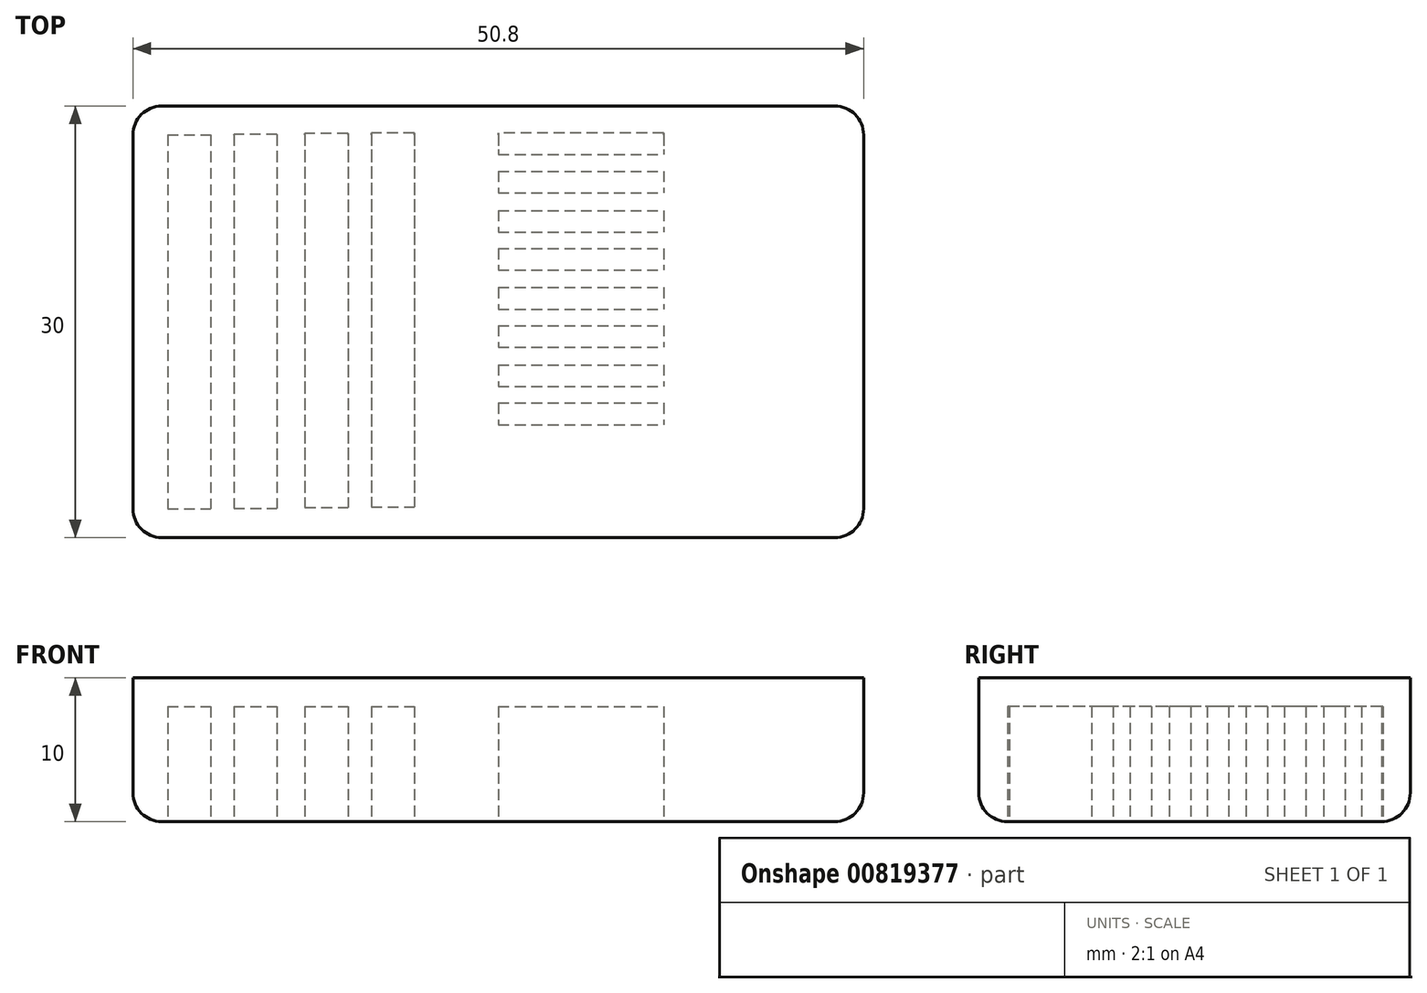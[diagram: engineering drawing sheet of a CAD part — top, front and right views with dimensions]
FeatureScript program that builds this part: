
annotation { "Feature Type Name" : "Feature", "Feature Type Description" : "" }
export const myFeature = defineFeature(function(context is Context, id is Id, definition is map)
    precondition{}
    {
        {
            var Q0;
            Q0=qCreatedBy(makeId("Top.planeOp"),FACE);
            var sketch = newSketch(context, id + "F0", { "sketchPlane" : qUnion([Q0])});
            skLineSegment(sketch, "E0.bottom", {"start": v(25.4, 15) * mm, "end": v(-25.4, 15) * mm});
            skLineSegment(sketch, "E0.top", {"start": v(25.4, -15) * mm, "end": v(-25.4, -15) * mm});
            skLineSegment(sketch, "E0.left", {"start": v(25.4, 15) * mm, "end": v(25.4, -15) * mm});
            skLineSegment(sketch, "E0.right", {"start": v(-25.4, 15) * mm, "end": v(-25.4, -15) * mm});
            skPoint(sketch, "E0.middle", {"position": v(0, 0) * mm});
            skSolve(sketch);
        }
        {
            var Q0;
            Q0=makeQuery(id+"F0.imprint","IMPRINT",FACE,{"disambiguationData":[TD([[makeQuery(id+"F0.imprint","IMPRINT",EDGE,{"derivedFrom":sQuery(id+"F0.wireOp",EDGE,"E0.bottom")}),1.0]])]});
            extrude(context, id + "F1", {"entities" : qUnion([Q0]), "depth" : 10 * mm, "offsetDistance" : 25.4 * mm});
        }
        {
            var Q0;
            Q0=qCreatedBy(makeId("Top.planeOp"),FACE);
            var sketch = newSketch(context, id + "F2", { "sketchPlane" : qUnion([Q0])});
            skLineSegment(sketch, "E1.bottom", {"start": v(-23, 13) * mm, "end": v(-20, 13) * mm});
            skLineSegment(sketch, "E1.top", {"start": v(-23, -13) * mm, "end": v(-20, -13) * mm});
            skLineSegment(sketch, "E1.left", {"start": v(-23, 13) * mm, "end": v(-23, -13) * mm});
            skLineSegment(sketch, "E1.right", {"start": v(-20, 13) * mm, "end": v(-20, -13) * mm});
            skPoint(sketch, "E1.middle", {"position": v(-21.5, 0) * mm});
            skLineSegment(sketch, "E2.bottom", {"start": v(-18.38, 13.03) * mm, "end": v(-15.38, 13.03) * mm});
            skLineSegment(sketch, "E2.top", {"start": v(-18.38, -12.97) * mm, "end": v(-15.38, -12.97) * mm});
            skLineSegment(sketch, "E2.left", {"start": v(-18.38, 13.03) * mm, "end": v(-18.38, -12.97) * mm});
            skLineSegment(sketch, "E2.right", {"start": v(-15.38, 13.03) * mm, "end": v(-15.38, -12.97) * mm});
            skPoint(sketch, "E2.middle", {"position": v(-16.88, 0.03) * mm});
            skLineSegment(sketch, "E3.bottom", {"start": v(-13.45, 13.1) * mm, "end": v(-10.45, 13.1) * mm});
            skLineSegment(sketch, "E3.top", {"start": v(-13.45, -12.9) * mm, "end": v(-10.45, -12.9) * mm});
            skLineSegment(sketch, "E3.left", {"start": v(-13.45, 13.1) * mm, "end": v(-13.45, -12.9) * mm});
            skLineSegment(sketch, "E3.right", {"start": v(-10.45, 13.1) * mm, "end": v(-10.45, -12.9) * mm});
            skPoint(sketch, "E3.middle", {"position": v(-11.95, 0.1) * mm});
            skLineSegment(sketch, "E4.bottom", {"start": v(-8.83, 13.12) * mm, "end": v(-5.83, 13.12) * mm});
            skLineSegment(sketch, "E4.top", {"start": v(-8.83, -12.88) * mm, "end": v(-5.83, -12.88) * mm});
            skLineSegment(sketch, "E4.left", {"start": v(-8.83, 13.12) * mm, "end": v(-8.83, -12.88) * mm});
            skLineSegment(sketch, "E4.right", {"start": v(-5.83, 13.12) * mm, "end": v(-5.83, -12.88) * mm});
            skPoint(sketch, "E4.middle", {"position": v(-7.33, 0.12) * mm});
            skLineSegment(sketch, "E5.bottom", {"start": v(0, 13.12) * mm, "end": v(11.5, 13.12) * mm});
            skLineSegment(sketch, "E5.top", {"start": v(0, 11.62) * mm, "end": v(11.5, 11.62) * mm});
            skLineSegment(sketch, "E5.left", {"start": v(0, 13.12) * mm, "end": v(0, 11.62) * mm});
            skLineSegment(sketch, "E5.right", {"start": v(11.5, 13.12) * mm, "end": v(11.5, 11.62) * mm});
            skLineSegment(sketch, "E6.bottom", {"start": v(0, 10.47) * mm, "end": v(11.5, 10.47) * mm});
            skLineSegment(sketch, "E6.top", {"start": v(0, 8.97) * mm, "end": v(11.5, 8.97) * mm});
            skLineSegment(sketch, "E6.left", {"start": v(0, 10.47) * mm, "end": v(0, 8.97) * mm});
            skLineSegment(sketch, "E6.right", {"start": v(11.5, 10.47) * mm, "end": v(11.5, 8.97) * mm});
            skLineSegment(sketch, "E7.bottom", {"start": v(0, 7.74) * mm, "end": v(11.5, 7.74) * mm});
            skLineSegment(sketch, "E7.top", {"start": v(0, 6.24) * mm, "end": v(11.5, 6.24) * mm});
            skLineSegment(sketch, "E7.left", {"start": v(0, 7.74) * mm, "end": v(0, 6.24) * mm});
            skLineSegment(sketch, "E7.right", {"start": v(11.5, 7.74) * mm, "end": v(11.5, 6.24) * mm});
            skLineSegment(sketch, "E8.bottom", {"start": v(0, 5.09) * mm, "end": v(11.5, 5.09) * mm});
            skLineSegment(sketch, "E8.top", {"start": v(0, 3.59) * mm, "end": v(11.5, 3.59) * mm});
            skLineSegment(sketch, "E8.left", {"start": v(0, 5.09) * mm, "end": v(0, 3.59) * mm});
            skLineSegment(sketch, "E8.right", {"start": v(11.5, 5.09) * mm, "end": v(11.5, 3.59) * mm});
            skLineSegment(sketch, "E9.bottom", {"start": v(0, 2.39) * mm, "end": v(11.5, 2.39) * mm});
            skLineSegment(sketch, "E9.top", {"start": v(0, 0.89) * mm, "end": v(11.5, 0.89) * mm});
            skLineSegment(sketch, "E9.left", {"start": v(0, 2.39) * mm, "end": v(0, 0.89) * mm});
            skLineSegment(sketch, "E9.right", {"start": v(11.5, 2.39) * mm, "end": v(11.5, 0.89) * mm});
            skLineSegment(sketch, "E10.bottom", {"start": v(0, -0.27) * mm, "end": v(11.5, -0.27) * mm});
            skLineSegment(sketch, "E10.top", {"start": v(0, -1.77) * mm, "end": v(11.5, -1.77) * mm});
            skLineSegment(sketch, "E10.left", {"start": v(0, -0.27) * mm, "end": v(0, -1.77) * mm});
            skLineSegment(sketch, "E10.right", {"start": v(11.5, -0.27) * mm, "end": v(11.5, -1.77) * mm});
            skLineSegment(sketch, "E11.bottom", {"start": v(0, -3) * mm, "end": v(11.5, -3) * mm});
            skLineSegment(sketch, "E11.top", {"start": v(0, -4.5) * mm, "end": v(11.5, -4.5) * mm});
            skLineSegment(sketch, "E11.left", {"start": v(0, -3) * mm, "end": v(0, -4.5) * mm});
            skLineSegment(sketch, "E11.right", {"start": v(11.5, -3) * mm, "end": v(11.5, -4.5) * mm});
            skLineSegment(sketch, "E12.bottom", {"start": v(0, -5.65) * mm, "end": v(11.5, -5.65) * mm});
            skLineSegment(sketch, "E12.top", {"start": v(0, -7.15) * mm, "end": v(11.5, -7.15) * mm});
            skLineSegment(sketch, "E12.left", {"start": v(0, -5.65) * mm, "end": v(0, -7.15) * mm});
            skLineSegment(sketch, "E12.right", {"start": v(11.5, -5.65) * mm, "end": v(11.5, -7.15) * mm});
            skSolve(sketch);
        }
        {
            var Q0;
            Q0=makeQuery(id+"F2.imprint","IMPRINT",FACE,{"disambiguationData":[TD([[makeQuery(id+"F2.imprint","IMPRINT",EDGE,{"derivedFrom":sQuery(id+"F2.wireOp",EDGE,"E4.bottom")}),-1.0]])]});
            var Q1;
            Q1=makeQuery(id+"F2.imprint","IMPRINT",FACE,{"disambiguationData":[TD([[makeQuery(id+"F2.imprint","IMPRINT",EDGE,{"derivedFrom":sQuery(id+"F2.wireOp",EDGE,"E3.bottom")}),-1.0]])]});
            var Q2;
            Q2=makeQuery(id+"F2.imprint","IMPRINT",FACE,{"disambiguationData":[TD([[makeQuery(id+"F2.imprint","IMPRINT",EDGE,{"derivedFrom":sQuery(id+"F2.wireOp",EDGE,"E2.bottom")}),-1.0]])]});
            var Q3;
            Q3=makeQuery(id+"F2.imprint","IMPRINT",FACE,{"disambiguationData":[TD([[makeQuery(id+"F2.imprint","IMPRINT",EDGE,{"derivedFrom":sQuery(id+"F2.wireOp",EDGE,"E1.bottom")}),-1.0]])]});
            var Q4;
            Q4=makeQuery(id+"F2.imprint","IMPRINT",FACE,{"disambiguationData":[TD([[makeQuery(id+"F2.imprint","IMPRINT",EDGE,{"derivedFrom":sQuery(id+"F2.wireOp",EDGE,"E8.bottom")}),-1.0]])]});
            var Q5;
            Q5=makeQuery(id+"F2.imprint","IMPRINT",FACE,{"disambiguationData":[TD([[makeQuery(id+"F2.imprint","IMPRINT",EDGE,{"derivedFrom":sQuery(id+"F2.wireOp",EDGE,"E7.bottom")}),-1.0]])]});
            var Q6;
            Q6=makeQuery(id+"F2.imprint","IMPRINT",FACE,{"disambiguationData":[TD([[makeQuery(id+"F2.imprint","IMPRINT",EDGE,{"derivedFrom":sQuery(id+"F2.wireOp",EDGE,"E6.bottom")}),-1.0]])]});
            var Q7;
            Q7=makeQuery(id+"F2.imprint","IMPRINT",FACE,{"disambiguationData":[TD([[makeQuery(id+"F2.imprint","IMPRINT",EDGE,{"derivedFrom":sQuery(id+"F2.wireOp",EDGE,"E5.bottom")}),-1.0]])]});
            var Q8;
            Q8=makeQuery(id+"F2.imprint","IMPRINT",FACE,{"disambiguationData":[TD([[makeQuery(id+"F2.imprint","IMPRINT",EDGE,{"derivedFrom":sQuery(id+"F2.wireOp",EDGE,"E9.bottom")}),-1.0]])]});
            var Q9;
            Q9=makeQuery(id+"F2.imprint","IMPRINT",FACE,{"disambiguationData":[TD([[makeQuery(id+"F2.imprint","IMPRINT",EDGE,{"derivedFrom":sQuery(id+"F2.wireOp",EDGE,"E10.bottom")}),-1.0]])]});
            var Q10;
            Q10=makeQuery(id+"F2.imprint","IMPRINT",FACE,{"disambiguationData":[TD([[makeQuery(id+"F2.imprint","IMPRINT",EDGE,{"derivedFrom":sQuery(id+"F2.wireOp",EDGE,"E11.bottom")}),-1.0]])]});
            var Q11;
            Q11=makeQuery(id+"F2.imprint","IMPRINT",FACE,{"disambiguationData":[TD([[makeQuery(id+"F2.imprint","IMPRINT",EDGE,{"derivedFrom":sQuery(id+"F2.wireOp",EDGE,"E12.bottom")}),-1.0]])]});
            extrude(context, id + "F3", {"entities" : qUnion([Q0, Q1, Q2, Q3, Q4, Q5, Q6, Q7, Q8, Q9, Q10, Q11]), "operationType" : NewBodyOperationType.REMOVE, "depth" : 8 * mm, "offsetDistance" : 25.4 * mm});
        }
        {
            var Q0;
            Q0=makeQuery(id+"F1.opExtrude","SWEPT_EDGE",EDGE,{"disambiguationData":[OSD([sQuery(id+"F0.wireOp",EDGE,"E0.bottom"),sQuery(id+"F0.wireOp",EDGE,"E0.left")])]});
            var Q1;
            Q1=makeQuery(id+"F1.opExtrude","CAP_EDGE",EDGE,{"disambiguationData":[OSD([sQuery(id+"F0.wireOp",EDGE,"E0.left")])],"isStart":true});
            var Q2;
            Q2=makeQuery(id+"F1.opExtrude","SWEPT_EDGE",EDGE,{"disambiguationData":[OSD([sQuery(id+"F0.wireOp",EDGE,"E0.top"),sQuery(id+"F0.wireOp",EDGE,"E0.left")])]});
            var Q3;
            Q3=makeQuery(id+"F1.opExtrude","CAP_EDGE",EDGE,{"disambiguationData":[OSD([sQuery(id+"F0.wireOp",EDGE,"E0.top")])],"isStart":true});
            var Q4;
            Q4=makeQuery(id+"F1.opExtrude","CAP_EDGE",EDGE,{"disambiguationData":[OSD([sQuery(id+"F0.wireOp",EDGE,"E0.right")])],"isStart":true});
            var Q5;
            Q5=makeQuery(id+"F1.opExtrude","SWEPT_EDGE",EDGE,{"disambiguationData":[OSD([sQuery(id+"F0.wireOp",EDGE,"E0.top"),sQuery(id+"F0.wireOp",EDGE,"E0.right")])]});
            var Q6;
            Q6=makeQuery(id+"F1.opExtrude","SWEPT_EDGE",EDGE,{"disambiguationData":[OSD([sQuery(id+"F0.wireOp",EDGE,"E0.bottom"),sQuery(id+"F0.wireOp",EDGE,"E0.right")])]});
            var Q7;
            Q7=makeQuery(id+"F1.opExtrude","CAP_EDGE",EDGE,{"disambiguationData":[OSD([sQuery(id+"F0.wireOp",EDGE,"E0.bottom")])],"isStart":true});
            fillet(context, id + "F4", {"entities" : qUnion([Q0, Q1, Q2, Q3, Q4, Q5, Q6, Q7]), "radius" : 2 * mm, "tangentPropagation" : true, "allowEdgeOverflow" : false});
        }
    });
